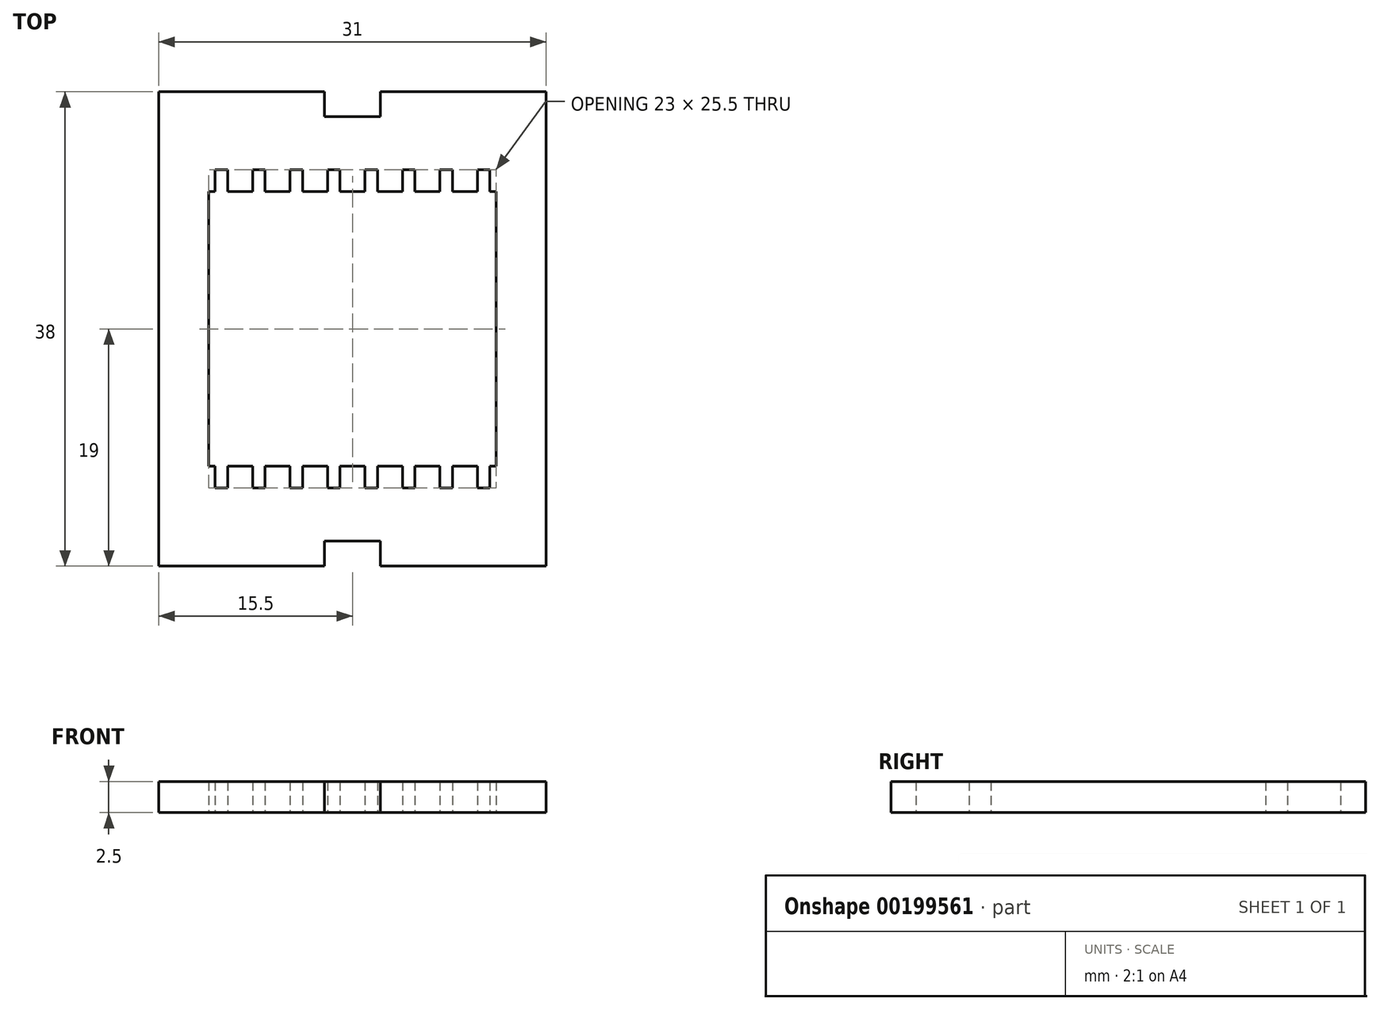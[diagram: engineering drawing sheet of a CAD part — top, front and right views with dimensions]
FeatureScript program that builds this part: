
annotation { "Feature Type Name" : "Feature", "Feature Type Description" : "" }
export const myFeature = defineFeature(function(context is Context, id is Id, definition is map)
    precondition{}
    {
        {
            var Q0;
            Q0=qCreatedBy(makeId("Top.planeOp"),FACE);
            var sketch = newSketch(context, id + "F0", { "sketchPlane" : qUnion([Q0])});
            skLineSegment(sketch, "E0.bottom", {"start": v(15.5, -19) * mm, "end": v(2.25, -19) * mm});
            skLineSegment(sketch, "E0.top", {"start": v(15.5, 19) * mm, "end": v(2.25, 19) * mm});
            skLineSegment(sketch, "E0.left", {"start": v(15.5, -19) * mm, "end": v(15.5, 19) * mm});
            skLineSegment(sketch, "E0.right", {"start": v(-15.5, -19) * mm, "end": v(-15.5, 19) * mm});
            skPoint(sketch, "E0.middle", {"position": v(0, 0) * mm});
            skLineSegment(sketch, "E1.bottom", {"start": v(2.25, -17) * mm, "end": v(-2.25, -17) * mm});
            skLineSegment(sketch, "E1.top", {"start": v(2.25, 17) * mm, "end": v(-2.25, 17) * mm});
            skLineSegment(sketch, "E1.left", {"start": v(15.5, -17) * mm, "end": v(15.5, 17) * mm});
            skLineSegment(sketch, "E1.right", {"start": v(-15.5, -17) * mm, "end": v(-15.5, 17) * mm});
            skLineSegment(sketch, "E2.bottom", {"start": v(-15.5, 19) * mm, "end": v(-2.25, 19) * mm});
            skLineSegment(sketch, "E2.top", {"start": v(-15.5, -19) * mm, "end": v(-2.25, -19) * mm});
            skLineSegment(sketch, "E2.left", {"start": v(-15.5, 19) * mm, "end": v(-15.5, -19) * mm});
            skLineSegment(sketch, "E2.right", {"start": v(-2.25, 19) * mm, "end": v(-2.25, 17) * mm});
            skLineSegment(sketch, "E3.left", {"start": v(15.5, 19) * mm, "end": v(15.5, -19) * mm});
            skLineSegment(sketch, "E3.right", {"start": v(2.25, 19) * mm, "end": v(2.25, 17) * mm});
            skLineSegment(sketch, "E4.trimOffspring", {"start": v(-2.25, -17) * mm, "end": v(-2.25, -19) * mm});
            skLineSegment(sketch, "E5.trimOffspring", {"start": v(2.25, -17) * mm, "end": v(2.25, -19) * mm});
            skLineSegment(sketch, "E6.trimOffspring", {"start": v(-2.25, 19) * mm, "end": v(-15.5, 19) * mm});
            skLineSegment(sketch, "E7.trimOffspring", {"start": v(-2.25, -19) * mm, "end": v(-15.5, -19) * mm});
            skLineSegment(sketch, "E8.left", {"start": v(11.5, -11) * mm, "end": v(11.5, 11) * mm});
            skLineSegment(sketch, "E8.right", {"start": v(-11.5, -11) * mm, "end": v(-11.5, 11) * mm});
            skLineSegment(sketch, "E9.bottom", {"start": v(11.5, -11) * mm, "end": v(11, -11) * mm});
            skLineSegment(sketch, "E9.top", {"start": v(11.5, 11) * mm, "end": v(11, 11) * mm});
            skPoint(sketch, "E10.orphan", {"position": v(11.5, -12.75) * mm});
            skLineSegment(sketch, "E11", {"start": v(-11, 12.75) * mm, "end": v(-10, 12.75) * mm});
            skLineSegment(sketch, "E12", {"start": v(-11, 12.75) * mm, "end": v(-11, 11) * mm});
            skLineSegment(sketch, "E13", {"start": v(-10, 12.75) * mm, "end": v(-10, 11) * mm});
            skLineSegment(sketch, "E14", {"start": v(-11, -12.75) * mm, "end": v(-11, -11) * mm});
            skLineSegment(sketch, "E15", {"start": v(-10, -12.75) * mm, "end": v(-10, -11) * mm});
            skLineSegment(sketch, "E16.trimOffspring", {"start": v(-11, -11) * mm, "end": v(-11.5, -11) * mm});
            skLineSegment(sketch, "E17.trimOffspring", {"start": v(-11, 11) * mm, "end": v(-11.5, 11) * mm});
            skLineSegment(sketch, "E18", {"start": v(-11, -12.75) * mm, "end": v(-10, -12.75) * mm});
            skLineSegment(sketch, "E19", {"start": v(-8, 12.75) * mm, "end": v(-7, 12.75) * mm});
            skLineSegment(sketch, "E20", {"start": v(-8, 12.75) * mm, "end": v(-8, 11) * mm});
            skLineSegment(sketch, "E21", {"start": v(-7, 12.75) * mm, "end": v(-7, 11) * mm});
            skLineSegment(sketch, "E22", {"start": v(-8, -12.75) * mm, "end": v(-7, -12.75) * mm});
            skLineSegment(sketch, "E23", {"start": v(-8, -12.75) * mm, "end": v(-8, -11) * mm});
            skLineSegment(sketch, "E24", {"start": v(-7, -12.75) * mm, "end": v(-7, -11) * mm});
            skLineSegment(sketch, "E25.trimOffspring", {"start": v(-8, -11) * mm, "end": v(-10, -11) * mm});
            skLineSegment(sketch, "E26.trimOffspring", {"start": v(-8, 11) * mm, "end": v(-10, 11) * mm});
            skLineSegment(sketch, "E27", {"start": v(-5, 12.75) * mm, "end": v(-4, 12.75) * mm});
            skLineSegment(sketch, "E28", {"start": v(-5, 12.75) * mm, "end": v(-5, 11) * mm});
            skLineSegment(sketch, "E29", {"start": v(-4, 12.75) * mm, "end": v(-4, 11) * mm});
            skLineSegment(sketch, "E30", {"start": v(-5, -12.75) * mm, "end": v(-4, -12.75) * mm});
            skLineSegment(sketch, "E31", {"start": v(-5, -12.75) * mm, "end": v(-5, -11) * mm});
            skLineSegment(sketch, "E32", {"start": v(-4, -12.75) * mm, "end": v(-4, -11) * mm});
            skLineSegment(sketch, "E33.trimOffspring", {"start": v(-5, -11) * mm, "end": v(-7, -11) * mm});
            skLineSegment(sketch, "E34.trimOffspring", {"start": v(-5, 11) * mm, "end": v(-7, 11) * mm});
            skLineSegment(sketch, "E35", {"start": v(-2, 12.75) * mm, "end": v(-1, 12.75) * mm});
            skLineSegment(sketch, "E36", {"start": v(1, 12.75) * mm, "end": v(2, 12.75) * mm});
            skLineSegment(sketch, "E37", {"start": v(4, 12.75) * mm, "end": v(5, 12.75) * mm});
            skLineSegment(sketch, "E38", {"start": v(7, 12.75) * mm, "end": v(8, 12.75) * mm});
            skLineSegment(sketch, "E39", {"start": v(10, 12.75) * mm, "end": v(11, 12.75) * mm});
            skLineSegment(sketch, "E40", {"start": v(-2, 12.75) * mm, "end": v(-2, 11) * mm});
            skLineSegment(sketch, "E41", {"start": v(-1, 12.75) * mm, "end": v(-1, 11) * mm});
            skLineSegment(sketch, "E42", {"start": v(1, 12.75) * mm, "end": v(1, 11) * mm});
            skLineSegment(sketch, "E43", {"start": v(2, 12.75) * mm, "end": v(2, 11) * mm});
            skLineSegment(sketch, "E44", {"start": v(4, 12.75) * mm, "end": v(4, 11) * mm});
            skLineSegment(sketch, "E45", {"start": v(5, 12.75) * mm, "end": v(5, 11) * mm});
            skLineSegment(sketch, "E46", {"start": v(7, 12.75) * mm, "end": v(7, 11) * mm});
            skLineSegment(sketch, "E47", {"start": v(8, 12.75) * mm, "end": v(8, 11) * mm});
            skLineSegment(sketch, "E48", {"start": v(10, 12.75) * mm, "end": v(10, 11) * mm});
            skLineSegment(sketch, "E49", {"start": v(11, 12.75) * mm, "end": v(11, 11) * mm});
            skLineSegment(sketch, "E50", {"start": v(-2, -12.75) * mm, "end": v(-1, -12.75) * mm});
            skLineSegment(sketch, "E51", {"start": v(1, -11) * mm, "end": v(1, -12.75) * mm});
            skLineSegment(sketch, "E52", {"start": v(1, -12.75) * mm, "end": v(2, -12.75) * mm});
            skLineSegment(sketch, "E53", {"start": v(4, -12.75) * mm, "end": v(5, -12.75) * mm});
            skLineSegment(sketch, "E54", {"start": v(10, -12.75) * mm, "end": v(11, -12.75) * mm});
            skLineSegment(sketch, "E55", {"start": v(7, -12.75) * mm, "end": v(8, -12.75) * mm});
            skLineSegment(sketch, "E56", {"start": v(-2, -12.75) * mm, "end": v(-2, -11) * mm});
            skLineSegment(sketch, "E57", {"start": v(-1, -12.75) * mm, "end": v(-1, -11) * mm});
            skLineSegment(sketch, "E58", {"start": v(2, -12.75) * mm, "end": v(2, -11) * mm});
            skLineSegment(sketch, "E59", {"start": v(4, -12.75) * mm, "end": v(4, -11) * mm});
            skLineSegment(sketch, "E60", {"start": v(5, -12.75) * mm, "end": v(5, -11) * mm});
            skLineSegment(sketch, "E61", {"start": v(7, -12.75) * mm, "end": v(7, -11) * mm});
            skLineSegment(sketch, "E62", {"start": v(8, -12.75) * mm, "end": v(8, -11) * mm});
            skLineSegment(sketch, "E63", {"start": v(10, -12.75) * mm, "end": v(10, -11) * mm});
            skLineSegment(sketch, "E64", {"start": v(11, -12.75) * mm, "end": v(11, -11) * mm});
            skLineSegment(sketch, "E65.trimOffspring", {"start": v(-2, -11) * mm, "end": v(-4, -11) * mm});
            skLineSegment(sketch, "E66.trimOffspring", {"start": v(1, -11) * mm, "end": v(-1, -11) * mm});
            skLineSegment(sketch, "E67.trimOffspring", {"start": v(4, -11) * mm, "end": v(2, -11) * mm});
            skLineSegment(sketch, "E68.trimOffspring", {"start": v(7, -11) * mm, "end": v(5, -11) * mm});
            skLineSegment(sketch, "E69.trimOffspring", {"start": v(10, -11) * mm, "end": v(8, -11) * mm});
            skLineSegment(sketch, "E70.trimOffspring", {"start": v(-2, 11) * mm, "end": v(-4, 11) * mm});
            skLineSegment(sketch, "E71.trimOffspring", {"start": v(1, 11) * mm, "end": v(-1, 11) * mm});
            skLineSegment(sketch, "E72.trimOffspring", {"start": v(4, 11) * mm, "end": v(2, 11) * mm});
            skLineSegment(sketch, "E73.trimOffspring", {"start": v(7, 11) * mm, "end": v(5, 11) * mm});
            skLineSegment(sketch, "E74.trimOffspring", {"start": v(10, 11) * mm, "end": v(8, 11) * mm});
            skSolve(sketch);
        }
        {
            var Q0;
            Q0=makeQuery(id+"F0.imprint","IMPRINT",FACE,{"disambiguationData":[TD([[makeQuery(id+"F0.imprint","IMPRINT",EDGE,{"derivedFrom":sQuery(id+"F0.wireOp",EDGE,"E1.bottom")}),-1.0]])]});
            extrude(context, id + "F1", {"entities" : qUnion([Q0]), "depth" : 2.5 * mm});
        }
    });
